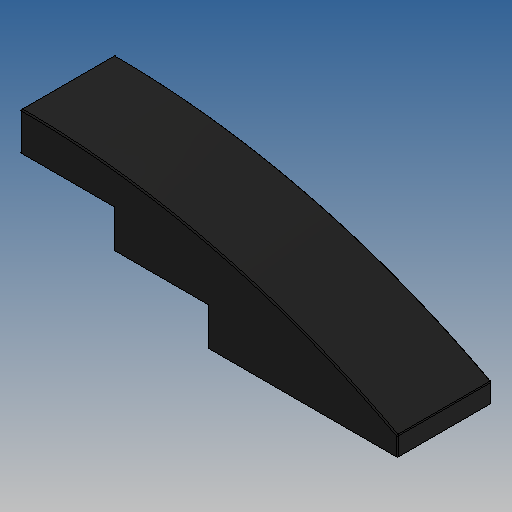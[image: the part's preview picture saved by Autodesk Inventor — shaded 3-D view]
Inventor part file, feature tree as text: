
AUTODESK INVENTOR PART (.ipt)
format: ipt  version: 2025 (Build 290162010, 162A)  size: 235,008 bytes
history: native  units: in
note: dims shown in document units (in); Inventor stores cm internally (conversion verified against a paired STEP export)
features: extrude x6, sketch x5, other x3, fillet x1
ambient origin geometry x8: Origin, YZ Plane, XZ Plane, XY Plane, X Axis, Y Axis, Z Axis, Center Point
bodies: Solid1 (feature_tree)
feature tree (15):
  extrude  "Extrusion1"  Depth=0.315in
  sketch  "Sketch10"  dims[d22=0.0039in d89=0.0in d90=0.0in]
  extrude  "Extrusion7"  Depth=0.378in TaperAngle=0.0deg
  extrude  "Extrusion8"  TaperAngle=0.0deg  [1 undecoded]
  extrude  "Extrusion2"  Depth=0.189in
  extrude  "Extrusion9"  Depth=0.063in
  extrude  "Extrusion10"  Depth=0.063in
  other  "Work Axis2"
  other  "Work Axis3"
  other  "Work Axis4"
  fillet  "Fillet1"  Radius=0.063in
  sketch  "Sketch2"  dims[d0=1.2598in d1=0.315in]
  sketch  "Sketch3"  dims[d4=0.378in d5=0.0in d7=0.0591in d11=0.3307in d12=0.0in]
  sketch  "Sketch11"  dims[d95=0.315in d96=0.0in d97=0.189in]
  sketch  "Sketch12"  dims[d98=0.0in d100=0.063in d102=0.063in d103=0.063in d104=0.063in d105=0.063in d107=0.063in d108=0.063in d109=0.189in d110=0.0in d112=0.0in d113=0.252in d114=0.126in d115=0.6299in d116=0.063in d118=0.0472in d119=0.0472in d120=0.3937in d121=0.0in d122=0.0472in d123=0.3937in d124=0.0in d125=0.0in d126=0.0in d127=0.0in d128=0.0in]
note: 1 required parameter value undecoded (feature->parameter linkage not recoverable at this tier; creation-order binding heuristic only, values carry confidence <= 0.55)
